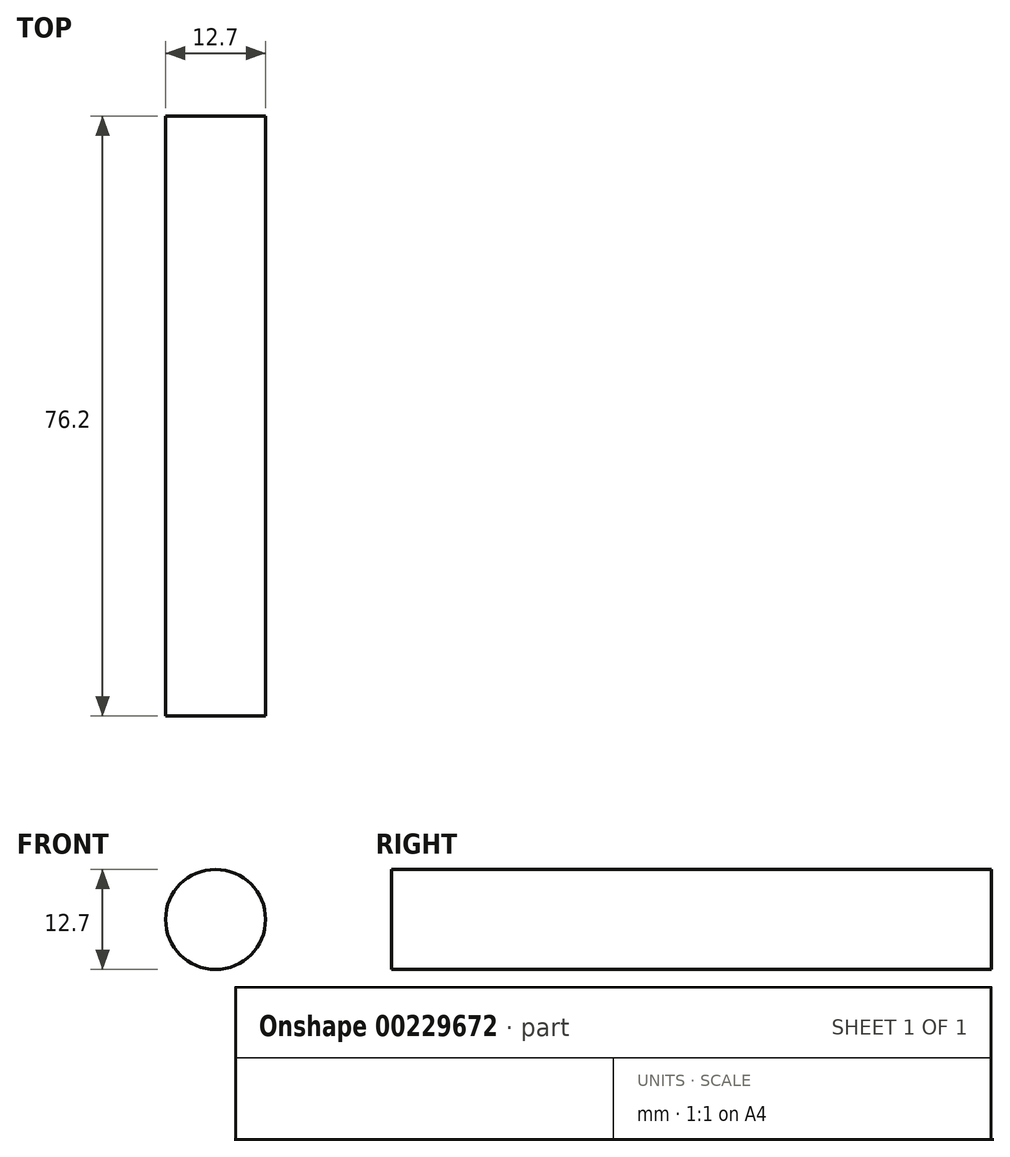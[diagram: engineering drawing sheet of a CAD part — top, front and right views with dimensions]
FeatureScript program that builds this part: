
annotation { "Feature Type Name" : "Feature", "Feature Type Description" : "" }
export const myFeature = defineFeature(function(context is Context, id is Id, definition is map)
    precondition{}
    {
        {
            var Q0;
            Q0=qCreatedBy(makeId("Front.planeOp"),FACE);
            var sketch = newSketch(context, id + "F0", { "sketchPlane" : qUnion([Q0])});
            skCircle(sketch, "E0", {"center": v(0, 0) * mm, "radius": 6.35 * mm});
            skPoint(sketch, "E1", {"position": v(0, 6.35) * mm});
            skSolve(sketch);
        }
        {
            var Q0;
            Q0 = qSketchRegion(id + "F0", true);
            extrude(context, id + "F1", {"entities" : qUnion([Q0]), "depth" : 76.2 * mm});
        }
    });
